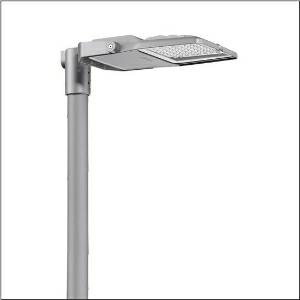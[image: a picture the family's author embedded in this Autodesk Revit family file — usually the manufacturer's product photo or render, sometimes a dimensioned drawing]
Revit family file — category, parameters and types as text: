
# Revit family: floodlight_fl_21_mini___pl33t_5xa7775c2f3a_8bfe
name_source: partatom
category: Lighting Fixtures
units: mm (PartAtom-declared; Revit-internal decimal feet)

## family parameters
Cut with Voids When Loaded = No
Host = Face
Light Source = No
Part Type = Normal
Room Calculation Point = No
Round Connector Dimension = Use Diameter
Shared = No

## types (1)
- --- (1 x LED, 12050 lm, 89 W, 3000K)
    Apparent Load = 89 VA
    CIE Flux Codes = 26 75 99 100 100
    Color Rendering = 70
    Color Temperature = 3000K
    Default Elevation = 1800 mm
    Description = Floodlight FL 21 mini, floodlight, primary light control with lens, of PMMA, primary optical cover: protective disc, of toughened safety glass, transparent, light distribution: PL33T, light emission: direct distribution, installation type: surface-mounted, LED, High Power LED, rated luminous flux: 12.050lm, luminous efficacy: 135lm/W, light colour: 730, colour temperature: 3000K, control gear: Smart Interface (Zhaga), control: flexible luminous flux parameterisation, time-dependent luminous flux control, constant luminous flux control, overheat protection, pre-setting: logarithmic dimming characteristic, with terminal, 6-pole, mains connection: 220..240V, AC, 50/60Hz, start of lifetime: 89W, end of service life: 94W, reduction: 43W, luminaire housing, of diecast aluminium, powder-coated, SITECO metallic grey (DB 702S), corrosivity category C5 mid according to DIN EN ISO 12944, suitable for swimming pools, chlorine-resistant, sealing non-destructively replaceable, please order mast flange separately, mast bracket, of steel, galvanised, powder-coated, SITECO metallic grey (DB 702S), Smart Interface above, protection rating (complete): IP66, insulation class (complete): insulation class II (safety insulation), certification: CE, ENEC, VDE, protection symbol: D, impact resistance: IK08, permissible operating ambient temperature: -40..+40°C, permissible operating ambient temperature for outdoor applications: -40..+50°C, standard: DIN EN 12944, LABS conformity tested according to VDMA 24364:2018-05, packaging unit: 1 piece

Light Distribution: PL33T
    Height = 70 mm
    Lamp = 1 x LED
    Lamp Light Flux = 12050 lm
    Lamp Power = 89 W
    Lamp count = 1
    Length = 485 mm
    Luminous efficacy = 135 lm/W
    Manufacturer = Siteco
    ModVariant = No
    Model = 5XA7775C2F3A
    Number of Poles = 1
    OnlyDefault = Yes
    Power Factor = 1
    Product Name = Floodlight FL 21 mini | PL33T
    Product group = floodlight | pylon annexe
    ProductGroupID = 6201
    Protection Class = Protection class II
    Protection Degree = IP 66
    RLX_Detail_Level = 1
    RLX_Emergency_Light_Flux = 0 lm
    RLX_Emergency_Type = 0
    RLX_Emergency_Type_DB = No
    RlxData = <blob elided: 100897 chars, md5=36ede454>
    Socket = socket
    Standby Power = 0 W
    System Light Flux = 12050 lm
    System Power = 89 W
    Type Comments = factory setting: luminous flux: 100 % | dim-lin: 254 | 456 mA
    Type Image = l_1007125.jpg
    URL = http://relux.com
    VarID = @adj_148033
    Voltage = 0 V
    Weight = 0.00 kg
    Width = 337 mm

## geometry (parser evidence)
native form markers: Blend x4, Sweep x12
no freeform markers — native parametric forms only
